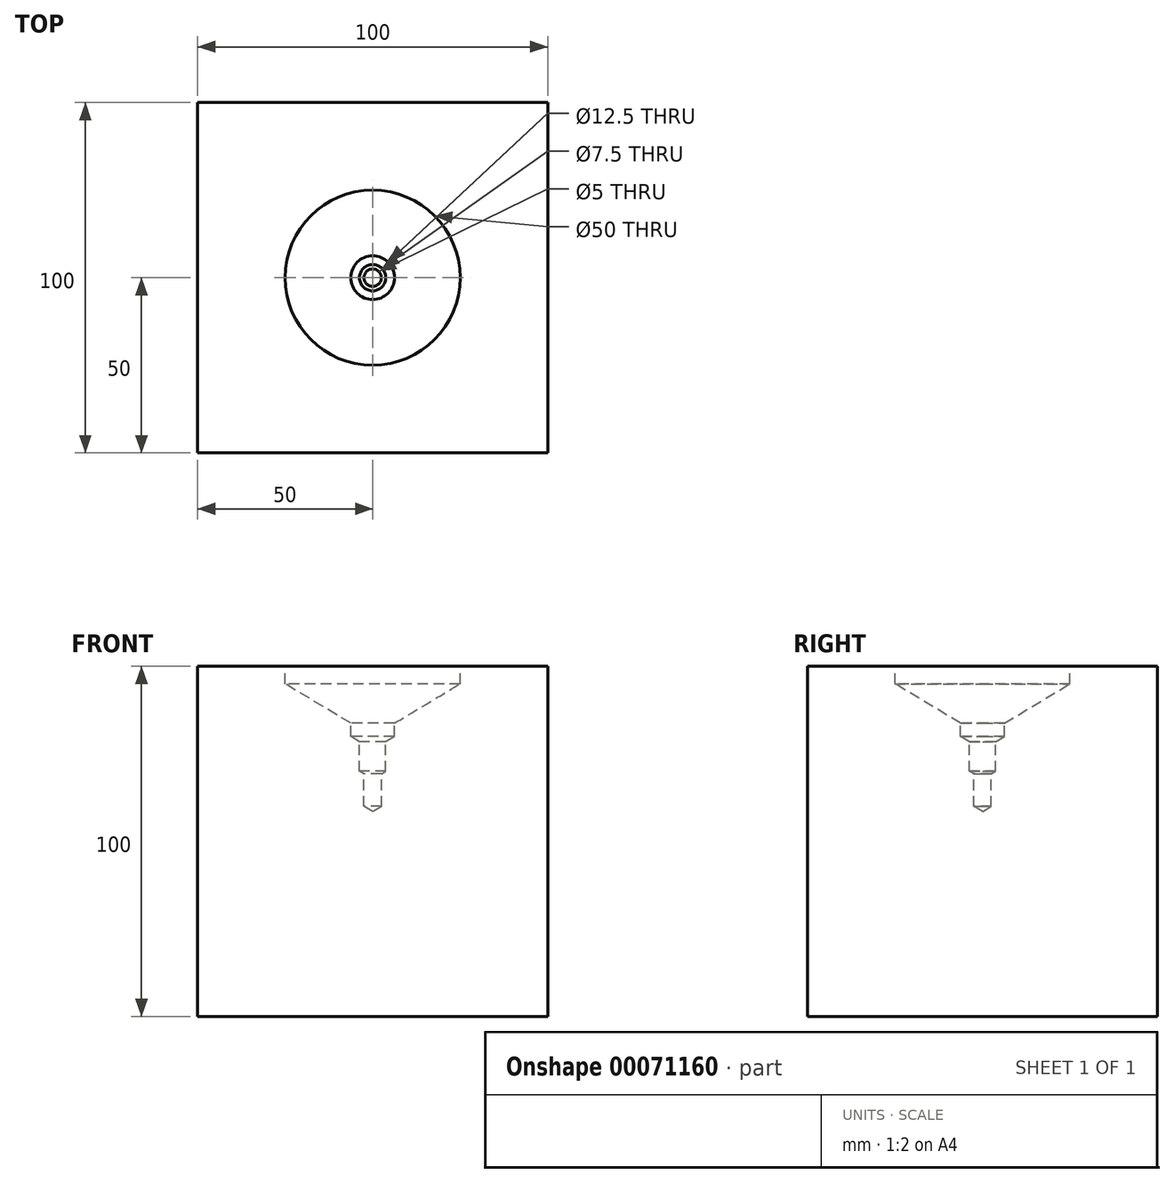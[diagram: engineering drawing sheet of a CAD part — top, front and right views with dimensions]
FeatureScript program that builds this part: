
annotation { "Feature Type Name" : "Feature", "Feature Type Description" : "" }
export const myFeature = defineFeature(function(context is Context, id is Id, definition is map)
    precondition{}
    {
        {
            var Q0;
            Q0=qCreatedBy(makeId("Front.planeOp"),FACE);
            var sketch = newSketch(context, id + "F0", { "sketchPlane" : qUnion([Q0])});
            skLineSegment(sketch, "E0.bottom", {"start": v(0, 0) * mm, "end": v(100, 0) * mm});
            skLineSegment(sketch, "E0.top", {"start": v(0, 100) * mm, "end": v(100, 100) * mm});
            skLineSegment(sketch, "E0.left", {"start": v(0, 0) * mm, "end": v(0, 100) * mm});
            skLineSegment(sketch, "E0.right", {"start": v(100, 0) * mm, "end": v(100, 100) * mm});
            skSolve(sketch);
        }
        {
            var Q0;
            Q0 = qSketchRegion(id + "F0", true);
            extrude(context, id + "F1", {"entities" : qUnion([Q0]), "depth" : 100 * mm});
        }
        {
            var Q0;
            Q0=makeQuery(id+"F1.opExtrude","SWEPT_FACE",FACE,{"disambiguationData":[OSD([sQuery(id+"F0.wireOp",EDGE,"E0.top")])]});
            var sketch = newSketch(context, id + "F2", { "sketchPlane" : qUnion([Q0])});
            skPoint(sketch, "E1", {"position": v(50, -50) * mm});
            skSolve(sketch);
        }
        {
            var Q0;
            Q0=sQuery(id+"F2.wireOp",VERTEX,"E1");
            var Q1;
            Q1=makeQuery(id+"F1.opExtrude","SWEPT_BODY",BODY,{"disambiguationData":[OSD([sQuery(id+"F0.wireOp",EDGE,"E0.bottom"),sQuery(id+"F0.wireOp",EDGE,"E0.top"),sQuery(id+"F0.wireOp",EDGE,"E0.left"),sQuery(id+"F0.wireOp",EDGE,"E0.right")])]});
            hole(context, id + "F3", {"style" : HoleStyle.SIMPLE, "holeDiameter" : 5 * mm, "endStyle" : HoleEndStyle.BLIND, "holeDepth" : 40 * mm, "locations" : qUnion([Q0]), "scope" : qUnion([Q1])});
        }
        {
            var Q0;
            Q0=sQuery(id+"F2.wireOp",VERTEX,"E1");
            var Q1;
            Q1=makeQuery(id+"F1.opExtrude","SWEPT_BODY",BODY,{"disambiguationData":[OSD([sQuery(id+"F0.wireOp",EDGE,"E0.bottom"),sQuery(id+"F0.wireOp",EDGE,"E0.top"),sQuery(id+"F0.wireOp",EDGE,"E0.left"),sQuery(id+"F0.wireOp",EDGE,"E0.right")])]});
            hole(context, id + "F4", {"style" : HoleStyle.SIMPLE, "holeDiameter" : 7.5 * mm, "endStyle" : HoleEndStyle.BLIND, "holeDepth" : 30 * mm, "locations" : qUnion([Q0]), "scope" : qUnion([Q1])});
        }
        {
            var Q0;
            Q0=sQuery(id+"F2.wireOp",VERTEX,"E1");
            var Q1;
            Q1=makeQuery(id+"F1.opExtrude","SWEPT_BODY",BODY,{"disambiguationData":[OSD([sQuery(id+"F0.wireOp",EDGE,"E0.bottom"),sQuery(id+"F0.wireOp",EDGE,"E0.top"),sQuery(id+"F0.wireOp",EDGE,"E0.left"),sQuery(id+"F0.wireOp",EDGE,"E0.right")])]});
            hole(context, id + "F5", {"style" : HoleStyle.SIMPLE, "holeDiameter" : 12.5 * mm, "endStyle" : HoleEndStyle.BLIND, "holeDepth" : 20 * mm, "locations" : qUnion([Q0]), "scope" : qUnion([Q1])});
        }
        {
            var Q0;
            Q0=sQuery(id+"F2.wireOp",VERTEX,"E1");
            var Q1;
            Q1=makeQuery(id+"F1.opExtrude","SWEPT_BODY",BODY,{"disambiguationData":[OSD([sQuery(id+"F0.wireOp",EDGE,"E0.bottom"),sQuery(id+"F0.wireOp",EDGE,"E0.top"),sQuery(id+"F0.wireOp",EDGE,"E0.left"),sQuery(id+"F0.wireOp",EDGE,"E0.right")])]});
            hole(context, id + "F6", {"style" : HoleStyle.SIMPLE, "holeDiameter" : 15 * mm, "endStyle" : HoleEndStyle.BLIND, "holeDepth" : 10 * mm, "locations" : qUnion([Q0]), "scope" : qUnion([Q1])});
        }
        {
            var Q0;
            Q0=sQuery(id+"F2.wireOp",VERTEX,"E1");
            var Q1;
            Q1=makeQuery(id+"F1.opExtrude","SWEPT_BODY",BODY,{"disambiguationData":[OSD([sQuery(id+"F0.wireOp",EDGE,"E0.bottom"),sQuery(id+"F0.wireOp",EDGE,"E0.top"),sQuery(id+"F0.wireOp",EDGE,"E0.left"),sQuery(id+"F0.wireOp",EDGE,"E0.right")])]});
            hole(context, id + "F7", {"style" : HoleStyle.SIMPLE, "holeDiameter" : 30 * mm, "endStyle" : HoleEndStyle.BLIND, "holeDepth" : 5 * mm, "locations" : qUnion([Q0]), "scope" : qUnion([Q1])});
        }
        {
            var Q0;
            Q0=sQuery(id+"F2.wireOp",VERTEX,"E1");
            var Q1;
            Q1=makeQuery(id+"F1.opExtrude","SWEPT_BODY",BODY,{"disambiguationData":[OSD([sQuery(id+"F0.wireOp",EDGE,"E0.bottom"),sQuery(id+"F0.wireOp",EDGE,"E0.top"),sQuery(id+"F0.wireOp",EDGE,"E0.left"),sQuery(id+"F0.wireOp",EDGE,"E0.right")])]});
            hole(context, id + "F8", {"style" : HoleStyle.SIMPLE, "holeDiameter" : 50 * mm, "endStyle" : HoleEndStyle.BLIND, "holeDepth" : 5 * mm, "locations" : qUnion([Q0]), "scope" : qUnion([Q1])});
        }
    });
